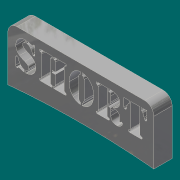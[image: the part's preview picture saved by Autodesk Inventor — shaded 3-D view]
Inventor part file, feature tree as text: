
AUTODESK INVENTOR PART (.ipt)
format: ipt  version: 2017 SP1 (Build 210196100, 196)  size: 490,496 bytes
history: native  units: in
note: dims shown in document units (in); Inventor stores cm internally (conversion verified against a paired STEP export)
features: extrude x2, sketch x2, fillet x1
ambient origin geometry x8: Origin, YZ Plane, XZ Plane, XY Plane, X Axis, Y Axis, Z Axis, Center Point
bodies: Solid1 (feature_tree)
feature tree (5):
  extrude  "Extrusion1"  Depth=1.5in
  extrude  "Extrusion2"  Depth=0.25in TaperAngle=0.0deg
  fillet  "Fillet1"  [1 undecoded]
  sketch  "Sketch1"  dims[d0=4.0in d1=1.5in]
  sketch  "Sketch2"  dims[d2=21.5in d3=0.5in d4=0.0in d5=0.0in d6=0.0in d7=0.25in]
note: 1 required parameter value undecoded (feature->parameter linkage not recoverable at this tier; creation-order binding heuristic only, values carry confidence <= 0.55)
